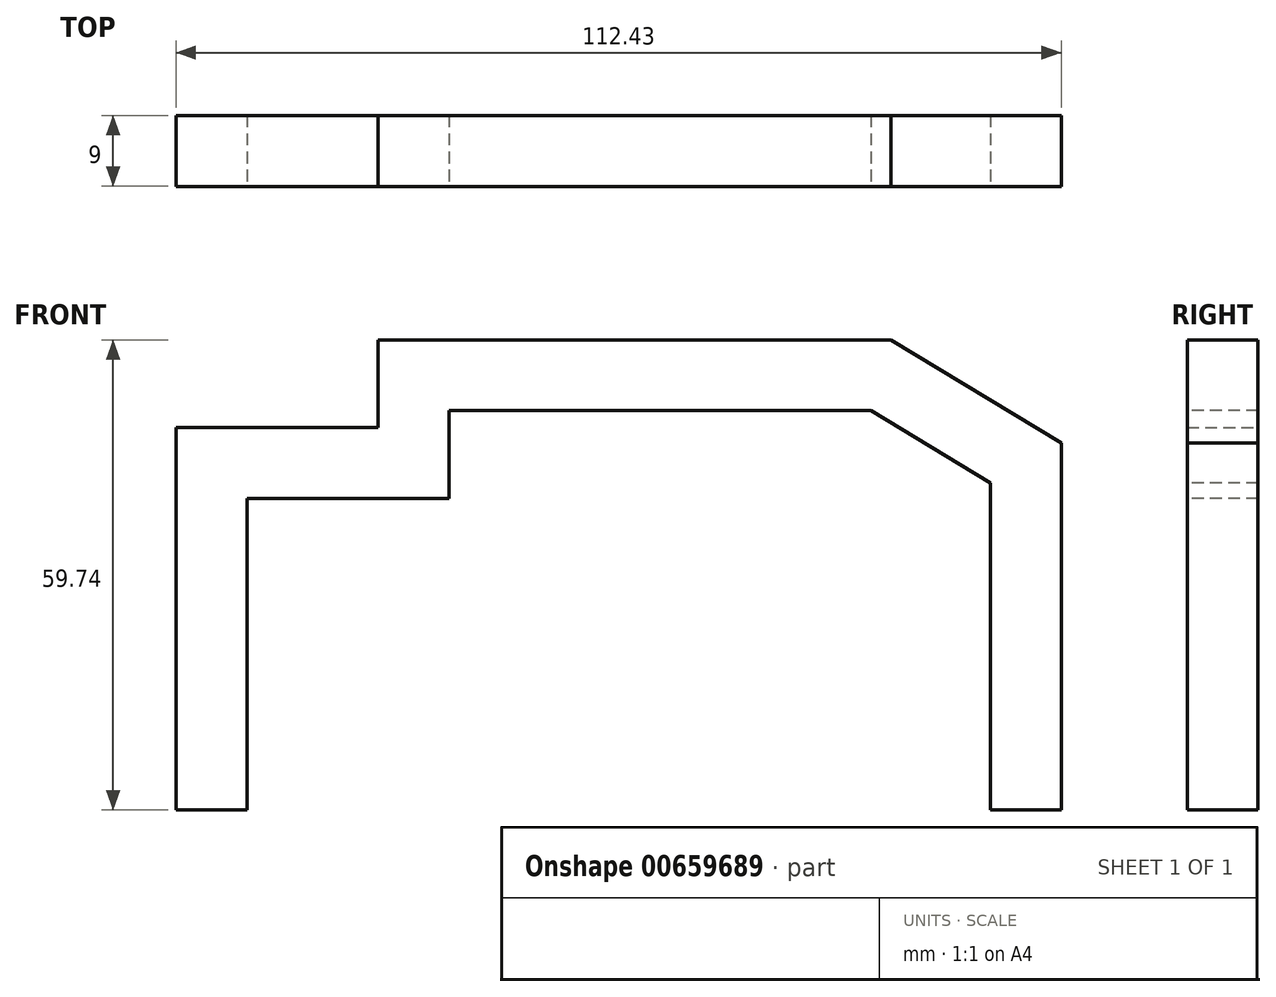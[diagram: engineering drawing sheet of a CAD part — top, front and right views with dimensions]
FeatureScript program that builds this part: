
annotation { "Feature Type Name" : "Feature", "Feature Type Description" : "" }
export const myFeature = defineFeature(function(context is Context, id is Id, definition is map)
    precondition{}
    {
        {
            var Q0;
            Q0=qCreatedBy(makeId("Front.planeOp"),FACE);
            var sketch = newSketch(context, id + "F0", { "sketchPlane" : qUnion([Q0])});
            skLineSegment(sketch, "E0", {"start": v(-53.96, 0) * mm, "end": v(-53.96, 44.07) * mm});
            skLineSegment(sketch, "E1", {"start": v(-53.96, 44.07) * mm, "end": v(-28.3, 44.07) * mm});
            skLineSegment(sketch, "E2", {"start": v(-28.3, 44.07) * mm, "end": v(-28.3, 55.23) * mm});
            skLineSegment(sketch, "E3", {"start": v(-28.3, 55.23) * mm, "end": v(31.04, 55.23) * mm});
            skLineSegment(sketch, "E4", {"start": v(31.04, 55.23) * mm, "end": v(49.46, 44.07) * mm});
            skLineSegment(sketch, "E5", {"start": v(49.46, 44.07) * mm, "end": v(49.46, 0) * mm});
            skSolve(sketch);
        }
        {
            var Q0;
            Q0=qCreatedBy(makeId("Top.planeOp"),FACE);
            var sketch = newSketch(context, id + "F1", { "sketchPlane" : qUnion([Q0])});
            skLineSegment(sketch, "E6.bottom", {"start": v(-49.46, -4.5) * mm, "end": v(-58.47, -4.5) * mm});
            skLineSegment(sketch, "E6.top", {"start": v(-49.46, 4.5) * mm, "end": v(-58.47, 4.5) * mm});
            skLineSegment(sketch, "E6.left", {"start": v(-49.46, -4.5) * mm, "end": v(-49.46, 4.5) * mm});
            skLineSegment(sketch, "E6.right", {"start": v(-58.47, -4.5) * mm, "end": v(-58.47, 4.5) * mm});
            skPoint(sketch, "E6.middle", {"position": v(-53.96, 0) * mm});
            skSolve(sketch);
        }
        {
            var Q0;
            Q0=makeQuery(id+"F1.imprint","IMPRINT",FACE,{"disambiguationData":[TD([[makeQuery(id+"F1.imprint","IMPRINT",EDGE,{"derivedFrom":sQuery(id+"F1.wireOp",EDGE,"E6.bottom")}),-1.0]])]});
            var Q1;
            Q1 = qConstructionFilter(qBodyType(qCreatedBy(id + "F0" ,EDGE), BodyType.WIRE), ConstructionObject.NO);
            sweep(context, id + "F2", {"profiles" : qUnion([Q0]), "path" : qUnion([Q1])});
        }
    });
